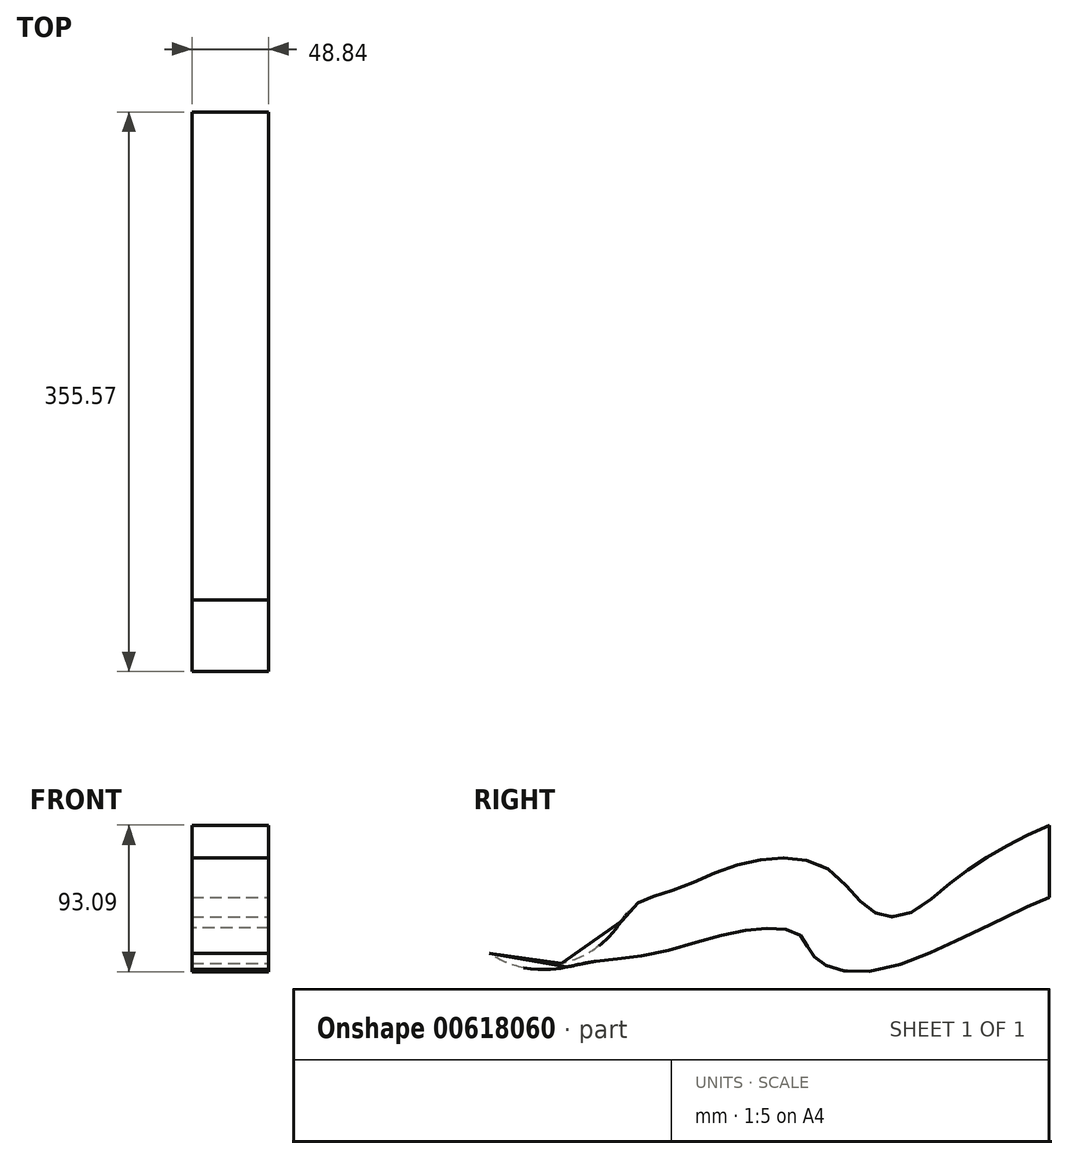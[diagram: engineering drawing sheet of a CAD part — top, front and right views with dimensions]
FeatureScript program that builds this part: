
annotation { "Feature Type Name" : "Feature", "Feature Type Description" : "" }
export const myFeature = defineFeature(function(context is Context, id is Id, definition is map)
    precondition{}
    {
        {
            var Q0;
            Q0=qCreatedBy(makeId("Front.planeOp"),FACE);
            var sketch = newSketch(context, id + "F0", { "sketchPlane" : qUnion([Q0])});
            skLineSegment(sketch, "E0.bottom", {"start": v(-25.22, 21.22) * mm, "end": v(23.62, 21.22) * mm});
            skLineSegment(sketch, "E0.top", {"start": v(-25.22, -24.65) * mm, "end": v(23.62, -24.65) * mm});
            skLineSegment(sketch, "E0.left", {"start": v(-25.22, 21.22) * mm, "end": v(-25.22, -24.65) * mm});
            skLineSegment(sketch, "E0.right", {"start": v(23.62, 21.22) * mm, "end": v(23.62, -24.65) * mm});
            skSolve(sketch);
        }
        {
            var Q0;
            Q0=qCreatedBy(makeId("Right.planeOp"),FACE);
            var sketch = newSketch(context, id + "F1", { "sketchPlane" : qUnion([Q0])});
            skFitSpline(sketch, "E1", {"points": [v(-53.88, 0) * mm, v(-135.19, -21.5) * mm, v(-190.33, -5.8) * mm, v(-281.95, -16.32) * mm, v(-323.04, -11.49) * mm, v(-323.82, -10.32) * mm], "startDerivative": vector(-322.67, -131.97) * mm, "endDerivative": vector(-8.26, 32.1) * mm});
            skSolve(sketch);
        }
        {
            var Q0;
            Q0=makeQuery(id+"F0.imprint","IMPRINT",FACE,{"disambiguationData":[TD([[makeQuery(id+"F0.imprint","IMPRINT",EDGE,{"derivedFrom":sQuery(id+"F0.wireOp",EDGE,"E0.bottom")}),-1.0]])]});
            var Q1;
            Q1=sQuery(id+"F1.wireOp",EDGE,"E1");
            sweep(context, id + "F2", {"profiles" : qUnion([Q0]), "path" : qUnion([Q1])});
        }
    });
